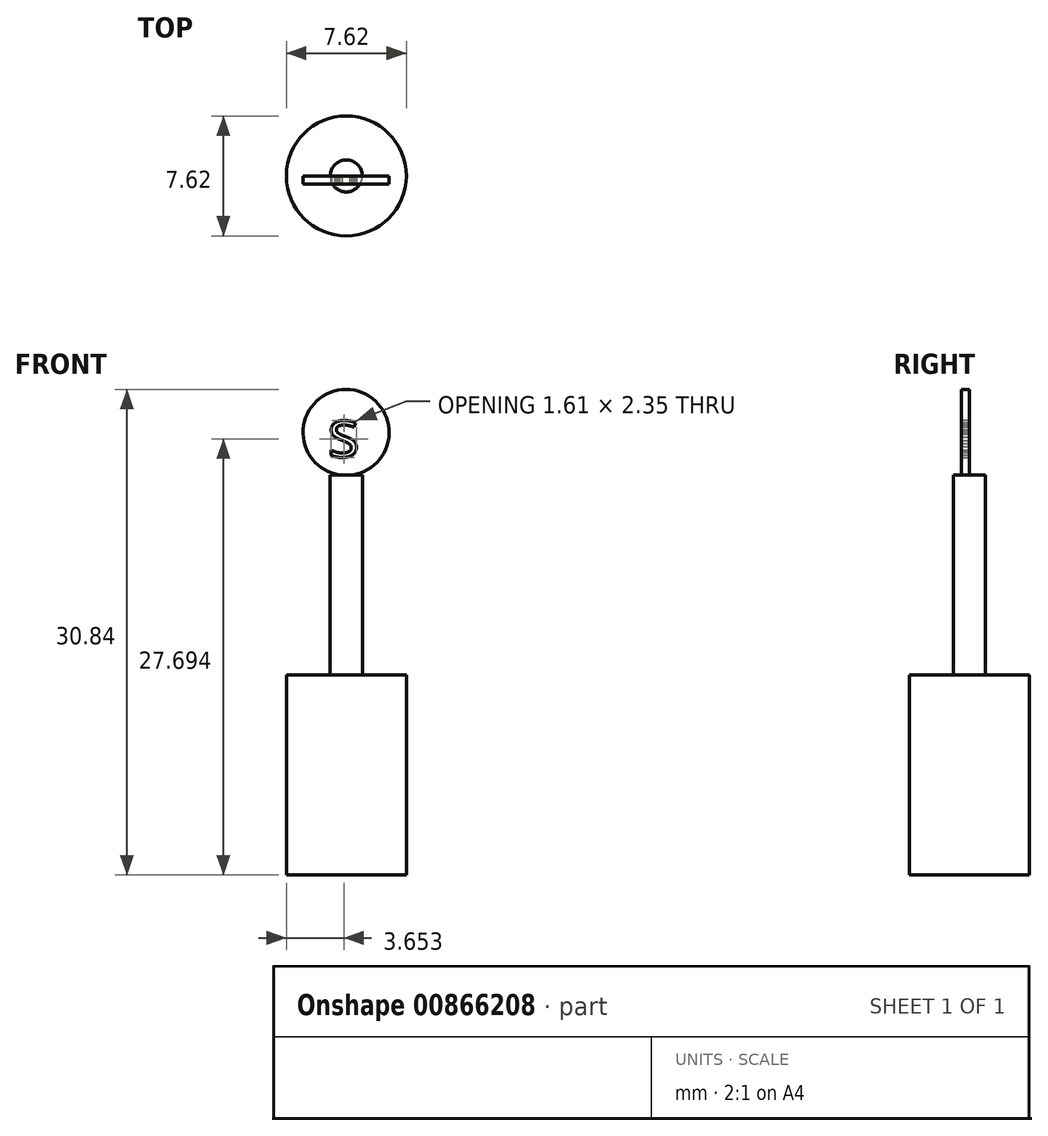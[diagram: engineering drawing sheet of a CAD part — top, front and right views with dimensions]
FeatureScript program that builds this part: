
annotation { "Feature Type Name" : "Feature", "Feature Type Description" : "" }
export const myFeature = defineFeature(function(context is Context, id is Id, definition is map)
    precondition{}
    {
        {
            var Q0;
            Q0=qCreatedBy(makeId("Top.planeOp"),FACE);
            var sketch = newSketch(context, id + "F0", { "sketchPlane" : qUnion([Q0])});
            skCircle(sketch, "E0", {"center": v(0, 0) * mm, "radius": 3.81 * mm});
            skSolve(sketch);
        }
        {
            var Q0;
            Q0 = qSketchRegion(id + "F0", true);
            extrude(context, id + "F1", {"entities" : qUnion([Q0]), "depth" : 12.7 * mm, "offsetDistance" : 25.4 * mm});
        }
        {
            var Q0;
            Q0=qCreatedBy(makeId("Top.planeOp"),FACE);
            var sketch = newSketch(context, id + "F2", { "sketchPlane" : qUnion([Q0])});
            skCircle(sketch, "E1", {"center": v(0, 0) * mm, "radius": 1.02 * mm});
            skSolve(sketch);
        }
        {
            var Q0;
            Q0 = qSketchRegion(id + "F2", true);
            extrude(context, id + "F3", {"entities" : qUnion([Q0]), "operationType" : NewBodyOperationType.ADD, "depth" : 25.4 * mm, "offsetDistance" : 25.4 * mm});
        }
        {
            var Q0;
            Q0=qCreatedBy(makeId("Front.planeOp"),FACE);
            var sketch = newSketch(context, id + "F4", { "sketchPlane" : qUnion([Q0])});
            skCircle(sketch, "E2", {"center": v(-0.01, 28.1) * mm, "radius": 2.73 * mm});
            skPoint(sketch, "E2.first.point", {"position": v(0, 30.84) * mm});
            skPoint(sketch, "E2.second.point", {"position": v(0, 25.37) * mm});
            skPoint(sketch, "E2.third.point", {"position": v(-2.74, 28) * mm});
            skSolve(sketch);
        }
        {
            var Q0;
            Q0 = qSketchRegion(id + "F4", true);
            extrude(context, id + "F5", {"entities" : qUnion([Q0]), "operationType" : NewBodyOperationType.ADD, "depth" : 0.5 * mm, "offsetDistance" : 25.4 * mm});
        }
        {
            var Q0;
            Q0=qCreatedBy(makeId("Front.planeOp"),FACE);
            var sketch = newSketch(context, id + "F6", { "sketchPlane" : qUnion([Q0])});
            skText(sketch, "E3", { "text": "s\n", "fontName": "OpenSans-Regular.ttf"});
            const initialGuessF6  = {"E3": [-0.00118, 0.02656, 1, 0, 0.00305]};
            skSetInitialGuess(sketch, initialGuessF6);
            skSolve(sketch);
        }
        {
            var Q0;
            Q0 = qSketchRegion(id + "F6", true);
            extrude(context, id + "F7", {"entities" : qUnion([Q0]), "operationType" : NewBodyOperationType.REMOVE, "endBound" : BoundingType.THROUGH_ALL, "depth" : 25.4 * mm, "offsetDistance" : 25.4 * mm});
        }
    });
